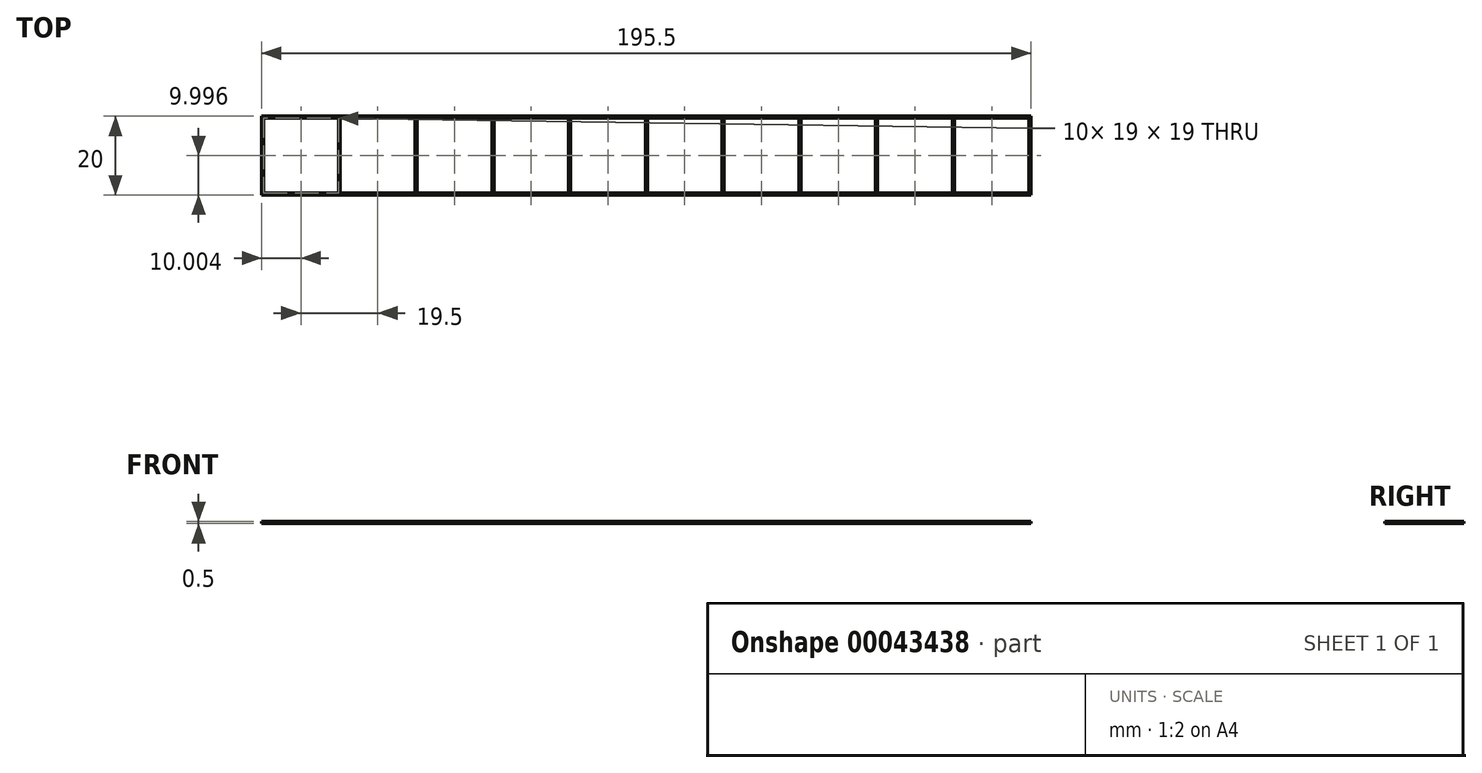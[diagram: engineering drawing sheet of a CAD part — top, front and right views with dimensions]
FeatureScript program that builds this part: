
annotation { "Feature Type Name" : "Feature", "Feature Type Description" : "" }
export const myFeature = defineFeature(function(context is Context, id is Id, definition is map)
    precondition{}
    {
        {
            var Q0;
            Q0=qCreatedBy(makeId("Top.planeOp"),FACE);
            var sketch = newSketch(context, id + "F0", { "sketchPlane" : qUnion([Q0])});
            skLineSegment(sketch, "E0.left", {"start": v(-64.95, 61.53) * mm, "end": v(-64.95, 41.53) * mm});
            skLineSegment(sketch, "E0.right", {"start": v(-44.95, 61.03) * mm, "end": v(-44.95, 42.03) * mm});
            skLineSegment(sketch, "E1.0", {"start": v(-64.45, 61.03) * mm, "end": v(-45.45, 61.03) * mm});
            skLineSegment(sketch, "E1.1", {"start": v(-64.45, 61.03) * mm, "end": v(-64.45, 42.03) * mm});
            skLineSegment(sketch, "E1.2", {"start": v(-64.45, 42.03) * mm, "end": v(-45.45, 42.03) * mm});
            skLineSegment(sketch, "E1.3", {"start": v(-45.45, 61.03) * mm, "end": v(-45.45, 42.03) * mm});
            skLineSegment(sketch, "E2.1.0.1", {"start": v(-44.95, 61.03) * mm, "end": v(-25.95, 61.03) * mm});
            skLineSegment(sketch, "E2.1.0.4", {"start": v(-44.95, 42.03) * mm, "end": v(-25.95, 42.03) * mm});
            skLineSegment(sketch, "E2.1.0.6", {"start": v(-25.95, 61.03) * mm, "end": v(-25.95, 42.03) * mm});
            skLineSegment(sketch, "E2.1.0.7", {"start": v(-25.45, 61.03) * mm, "end": v(-25.45, 42.03) * mm});
            skLineSegment(sketch, "E2.2.0.1", {"start": v(-25.45, 61.03) * mm, "end": v(-6.45, 61.03) * mm});
            skLineSegment(sketch, "E2.2.0.3", {"start": v(-25.45, 61.03) * mm, "end": v(-25.45, 42.03) * mm});
            skLineSegment(sketch, "E2.2.0.4", {"start": v(-25.45, 42.03) * mm, "end": v(-6.45, 42.03) * mm});
            skLineSegment(sketch, "E2.2.0.6", {"start": v(-6.45, 61.03) * mm, "end": v(-6.45, 42.03) * mm});
            skLineSegment(sketch, "E2.2.0.7", {"start": v(-5.95, 61.03) * mm, "end": v(-5.95, 42.03) * mm});
            skLineSegment(sketch, "E2.3.0.1", {"start": v(-5.95, 61.03) * mm, "end": v(13.05, 61.03) * mm});
            skLineSegment(sketch, "E2.3.0.2", {"start": v(-6.45, 61.03) * mm, "end": v(-6.45, 42.03) * mm});
            skLineSegment(sketch, "E2.3.0.3", {"start": v(-5.95, 61.03) * mm, "end": v(-5.95, 42.03) * mm});
            skLineSegment(sketch, "E2.3.0.4", {"start": v(-5.95, 42.03) * mm, "end": v(13.05, 42.03) * mm});
            skLineSegment(sketch, "E2.3.0.6", {"start": v(13.05, 61.03) * mm, "end": v(13.05, 42.03) * mm});
            skLineSegment(sketch, "E2.3.0.7", {"start": v(13.55, 61.03) * mm, "end": v(13.55, 42.03) * mm});
            skLineSegment(sketch, "E2.4.0.1", {"start": v(13.55, 61.03) * mm, "end": v(32.55, 61.03) * mm});
            skLineSegment(sketch, "E2.4.0.2", {"start": v(13.05, 61.03) * mm, "end": v(13.05, 42.03) * mm});
            skLineSegment(sketch, "E2.4.0.3", {"start": v(13.55, 61.03) * mm, "end": v(13.55, 42.03) * mm});
            skLineSegment(sketch, "E2.4.0.4", {"start": v(13.55, 42.03) * mm, "end": v(32.55, 42.03) * mm});
            skLineSegment(sketch, "E2.4.0.6", {"start": v(32.55, 61.03) * mm, "end": v(32.55, 42.03) * mm});
            skLineSegment(sketch, "E2.4.0.7", {"start": v(33.05, 61.03) * mm, "end": v(33.05, 42.03) * mm});
            skLineSegment(sketch, "E2.5.0.1", {"start": v(33.05, 61.03) * mm, "end": v(52.05, 61.03) * mm});
            skLineSegment(sketch, "E2.5.0.2", {"start": v(32.55, 61.03) * mm, "end": v(32.55, 42.03) * mm});
            skLineSegment(sketch, "E2.5.0.3", {"start": v(33.05, 61.03) * mm, "end": v(33.05, 42.03) * mm});
            skLineSegment(sketch, "E2.5.0.4", {"start": v(33.05, 42.03) * mm, "end": v(52.05, 42.03) * mm});
            skLineSegment(sketch, "E2.5.0.6", {"start": v(52.05, 61.03) * mm, "end": v(52.05, 42.03) * mm});
            skLineSegment(sketch, "E2.5.0.7", {"start": v(52.55, 61.03) * mm, "end": v(52.55, 42.03) * mm});
            skLineSegment(sketch, "E2.6.0.1", {"start": v(52.55, 61.03) * mm, "end": v(71.55, 61.03) * mm});
            skLineSegment(sketch, "E2.6.0.3", {"start": v(52.55, 61.03) * mm, "end": v(52.55, 42.03) * mm});
            skLineSegment(sketch, "E2.6.0.4", {"start": v(52.55, 42.03) * mm, "end": v(71.55, 42.03) * mm});
            skLineSegment(sketch, "E2.6.0.6", {"start": v(71.55, 61.03) * mm, "end": v(71.55, 42.03) * mm});
            skLineSegment(sketch, "E2.6.0.7", {"start": v(72.05, 61.03) * mm, "end": v(72.05, 42.03) * mm});
            skLineSegment(sketch, "E2.7.0.1", {"start": v(72.05, 61.03) * mm, "end": v(91.05, 61.03) * mm});
            skLineSegment(sketch, "E2.7.0.2", {"start": v(71.55, 61.03) * mm, "end": v(71.55, 42.03) * mm});
            skLineSegment(sketch, "E2.7.0.3", {"start": v(72.05, 61.03) * mm, "end": v(72.05, 42.03) * mm});
            skLineSegment(sketch, "E2.7.0.4", {"start": v(72.05, 42.03) * mm, "end": v(91.05, 42.03) * mm});
            skLineSegment(sketch, "E2.7.0.6", {"start": v(91.05, 61.03) * mm, "end": v(91.05, 42.03) * mm});
            skLineSegment(sketch, "E2.8.0.1", {"start": v(91.55, 61.03) * mm, "end": v(110.55, 61.03) * mm});
            skLineSegment(sketch, "E2.8.0.2", {"start": v(91.05, 61.03) * mm, "end": v(91.05, 42.03) * mm});
            skLineSegment(sketch, "E2.8.0.3", {"start": v(91.55, 61.03) * mm, "end": v(91.55, 42.03) * mm});
            skLineSegment(sketch, "E2.8.0.4", {"start": v(91.55, 42.03) * mm, "end": v(110.55, 42.03) * mm});
            skLineSegment(sketch, "E2.8.0.6", {"start": v(110.55, 61.03) * mm, "end": v(110.55, 42.03) * mm});
            skLineSegment(sketch, "E2.8.0.7", {"start": v(111.05, 61.03) * mm, "end": v(111.05, 42.03) * mm});
            skLineSegment(sketch, "E2.9.0.1", {"start": v(111.05, 61.03) * mm, "end": v(130.05, 61.03) * mm});
            skLineSegment(sketch, "E2.9.0.2", {"start": v(110.55, 61.03) * mm, "end": v(110.55, 42.03) * mm});
            skLineSegment(sketch, "E2.9.0.3", {"start": v(111.05, 61.03) * mm, "end": v(111.05, 42.03) * mm});
            skLineSegment(sketch, "E2.9.0.4", {"start": v(111.05, 42.03) * mm, "end": v(130.05, 42.03) * mm});
            skLineSegment(sketch, "E2.9.0.6", {"start": v(130.05, 61.03) * mm, "end": v(130.05, 42.03) * mm});
            skLineSegment(sketch, "E2.9.0.7", {"start": v(130.55, 61.53) * mm, "end": v(130.55, 41.53) * mm});
            skPoint(sketch, "E3.orphan", {"position": v(32.55, 61.53) * mm});
            skPoint(sketch, "E4.orphan", {"position": v(13.55, 61.53) * mm});
            skPoint(sketch, "E5.orphan", {"position": v(52.55, 61.53) * mm});
            skPoint(sketch, "E6.orphan", {"position": v(91.55, 41.53) * mm});
            skPoint(sketch, "E7.orphan", {"position": v(71.55, 41.53) * mm});
            skPoint(sketch, "E8.orphan", {"position": v(72.05, 41.53) * mm});
            skPoint(sketch, "E9.orphan", {"position": v(33.05, 41.53) * mm});
            skPoint(sketch, "E10.orphan", {"position": v(-5.95, 41.53) * mm});
            skLineSegment(sketch, "E11", {"start": v(130.55, 61.53) * mm, "end": v(-64.95, 61.53) * mm});
            skLineSegment(sketch, "E12", {"start": v(-64.95, 41.53) * mm, "end": v(130.55, 41.53) * mm});
            skSolve(sketch);
        }
        {
            var Q0;
            Q0=makeQuery(id+"F0.imprint","IMPRINT",FACE,{"disambiguationData":[TD([[makeQuery(id+"F0.imprint","IMPRINT",EDGE,{"derivedFrom":sQuery(id+"F0.wireOp",EDGE,"E0.left")}),1.0]])]});
            extrude(context, id + "F1", {"entities" : qUnion([Q0]), "depth" : 0.5 * mm});
        }
    });
